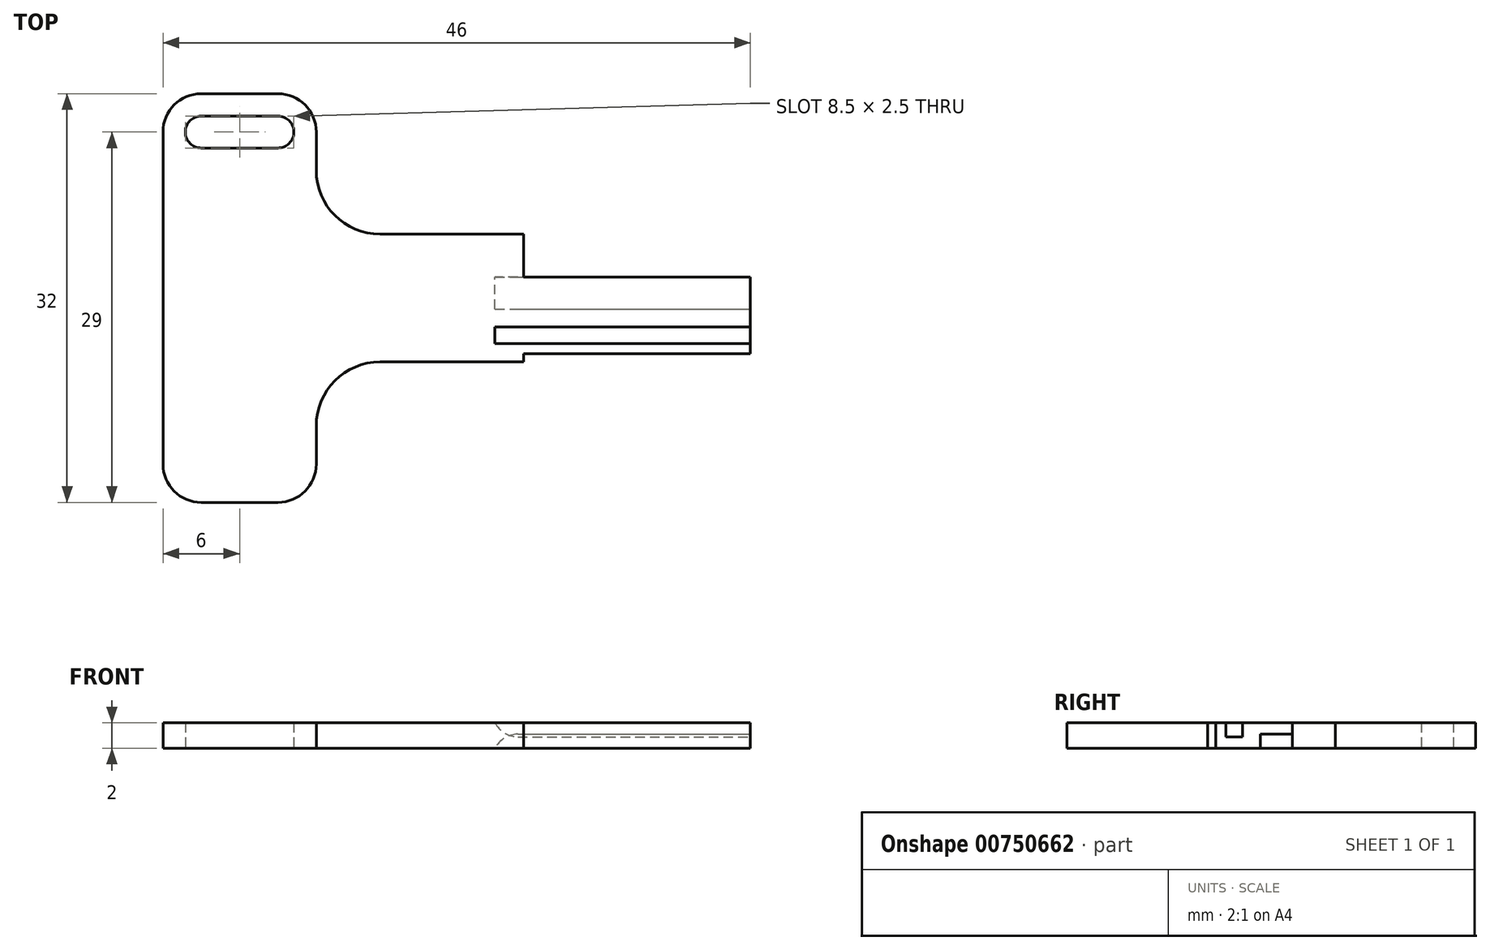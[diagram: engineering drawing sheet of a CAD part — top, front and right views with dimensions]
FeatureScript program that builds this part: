
annotation { "Feature Type Name" : "Feature", "Feature Type Description" : "" }
export const myFeature = defineFeature(function(context is Context, id is Id, definition is map)
    precondition{}
    {
        {
            var Q0;
            Q0=qCreatedBy(makeId("Top.planeOp"),FACE);
            var sketch = newSketch(context, id + "F0", { "sketchPlane" : qUnion([Q0])});
            skLineSegment(sketch, "E0.bottom", {"start": v(3, 0) * mm, "end": v(9, 0) * mm});
            skLineSegment(sketch, "E0.top", {"start": v(3, 32) * mm, "end": v(9, 32) * mm});
            skLineSegment(sketch, "E0.left", {"start": v(0, 3) * mm, "end": v(0, 29) * mm});
            skLineSegment(sketch, "E0.right", {"start": v(46, 11.65) * mm, "end": v(46, 17.65) * mm});
            skLineSegment(sketch, "E1", {"start": v(12, 29) * mm, "end": v(12, 26) * mm});
            skLineSegment(sketch, "E2", {"start": v(17, 21) * mm, "end": v(28.25, 21) * mm});
            skLineSegment(sketch, "E3", {"start": v(12, 3) * mm, "end": v(12, 6) * mm});
            skLineSegment(sketch, "E4", {"start": v(17, 11) * mm, "end": v(28.25, 11) * mm});
            skLineSegment(sketch, "E5", {"start": v(46, 11.65) * mm, "end": v(28.25, 11.65) * mm});
            skLineSegment(sketch, "E6", {"start": v(28.25, 11.65) * mm, "end": v(28.25, 11) * mm});
            skLineSegment(sketch, "E7", {"start": v(28.25, 21) * mm, "end": v(28.25, 17.65) * mm});
            skLineSegment(sketch, "E8", {"start": v(28.25, 17.65) * mm, "end": v(46, 17.65) * mm});
            skPoint(sketch, "E9.visualSharp", {"position": v(12, 21) * mm});
            skArc(sketch, "E9.filletArc", {"start": v(12, 26) * mm, "mid": v(13.46, 22.46) * mm, "end": v(17, 21) * mm});
            skPoint(sketch, "E10.visualSharp", {"position": v(12, 11) * mm});
            skArc(sketch, "E10.filletArc", {"start": v(17, 11) * mm, "mid": v(13.46, 9.54) * mm, "end": v(12, 6) * mm});
            skPoint(sketch, "E11.visualSharp", {"position": v(12, 32) * mm});
            skArc(sketch, "E11.filletArc", {"start": v(12, 29) * mm, "mid": v(11.12, 31.12) * mm, "end": v(9, 32) * mm});
            skPoint(sketch, "E12.visualSharp", {"position": v(0, 32) * mm});
            skArc(sketch, "E12.filletArc", {"start": v(3, 32) * mm, "mid": v(0.88, 31.12) * mm, "end": v(0, 29) * mm});
            skPoint(sketch, "E13.visualSharp", {"position": v(0, 0) * mm});
            skArc(sketch, "E13.filletArc", {"start": v(0, 3) * mm, "mid": v(0.88, 0.88) * mm, "end": v(3, 0) * mm});
            skPoint(sketch, "E14.newPointA", {"position": v(12, 0) * mm});
            skArc(sketch, "E14.filletArc", {"start": v(9, 0) * mm, "mid": v(11.12, 0.88) * mm, "end": v(12, 3) * mm});
            skArc(sketch, "E15", {"start": v(3, 30.25) * mm, "mid": v(1.75, 29) * mm, "end": v(3, 27.75) * mm});
            skArc(sketch, "E16", {"start": v(9, 27.75) * mm, "mid": v(10.25, 29) * mm, "end": v(9, 30.25) * mm});
            skLineSegment(sketch, "E17.top", {"start": v(3, 30.25) * mm, "end": v(9, 30.25) * mm});
            skLineSegment(sketch, "E18.top", {"start": v(3, 27.75) * mm, "end": v(9, 27.75) * mm});
            skSolve(sketch);
        }
        {
            var Q0;
            Q0 = qSketchRegion(id + "F0", true);
            extrude(context, id + "F1", {"entities" : qUnion([Q0]), "depth" : 2 * mm, "offsetDistance" : 25 * mm});
        }
        {
            var Q0;
            Q0=makeQuery(id+"F1.opExtrude","SWEPT_FACE",FACE,{"disambiguationData":[OSD([sQuery(id+"F0.wireOp",EDGE,"E0.right")])]});
            var sketch = newSketch(context, id + "F2", { "sketchPlane" : qUnion([Q0])});
            skLineSegment(sketch, "E19", {"start": v(11.65, 2) * mm, "end": v(12.45, 2) * mm, "construction": true});
            skLineSegment(sketch, "E20.bottom", {"start": v(12.45, 2) * mm, "end": v(13.75, 2) * mm});
            skLineSegment(sketch, "E20.top", {"start": v(12.45, 0.9) * mm, "end": v(13.75, 0.9) * mm});
            skLineSegment(sketch, "E20.left", {"start": v(12.45, 2) * mm, "end": v(12.45, 0.9) * mm});
            skLineSegment(sketch, "E20.right", {"start": v(13.75, 2) * mm, "end": v(13.75, 0.9) * mm});
            skLineSegment(sketch, "E21", {"start": v(11.65, 0) * mm, "end": v(15.15, 0) * mm});
            skLineSegment(sketch, "E22.bottom", {"start": v(15.15, 0) * mm, "end": v(17.65, 0) * mm});
            skLineSegment(sketch, "E22.top", {"start": v(15.15, 1.1) * mm, "end": v(17.65, 1.1) * mm});
            skLineSegment(sketch, "E22.left", {"start": v(15.15, 0) * mm, "end": v(15.15, 1.1) * mm});
            skLineSegment(sketch, "E22.right", {"start": v(17.65, 0) * mm, "end": v(17.65, 1.1) * mm});
            skSolve(sketch);
        }
        {
            var Q0;
            Q0=makeQuery(id+"F2.imprint","IMPRINT",FACE,{"disambiguationData":[TD([[makeQuery(id+"F2.imprint","IMPRINT",EDGE,{"derivedFrom":sQuery(id+"F2.wireOp",EDGE,"E20.bottom")}),-1.0]])]});
            var Q1;
            Q1=makeQuery(id+"F2.imprint","IMPRINT",FACE,{"disambiguationData":[TD([[makeQuery(id+"F2.imprint","IMPRINT",EDGE,{"derivedFrom":sQuery(id+"F2.wireOp",EDGE,"E22.bottom")}),1.0]])]});
            extrude(context, id + "F3", {"entities" : qUnion([Q0, Q1]), "operationType" : NewBodyOperationType.REMOVE, "oppositeDirection" : true, "depth" : 20 * mm, "offsetDistance" : 25 * mm});
        }
        {
            var Q0;
            Q0=makeQuery(id+"F3.boolean.opBoolean","COPY",EDGE,{"derivedFrom":makeQuery(id+"F3.opExtrude","CAP_EDGE",EDGE,{"disambiguationData":[OSD([sQuery(id+"F2.wireOp",EDGE,"E20.top")])],"isStart":false})});
            fillet(context, id + "F4", {"entities" : qUnion([Q0]), "radius" : 2 * mm, "tangentPropagation" : true, "allowEdgeOverflow" : false});
        }
        {
            var Q0;
            Q0=makeQuery(id+"F3.boolean.opBoolean","COPY",EDGE,{"derivedFrom":makeQuery(id+"F3.opExtrude","CAP_EDGE",EDGE,{"disambiguationData":[OSD([sQuery(id+"F2.wireOp",EDGE,"E22.top")])],"isStart":false})});
            fillet(context, id + "F5", {"entities" : qUnion([Q0]), "radius" : 2 * mm, "tangentPropagation" : true, "allowEdgeOverflow" : false});
        }
    });
